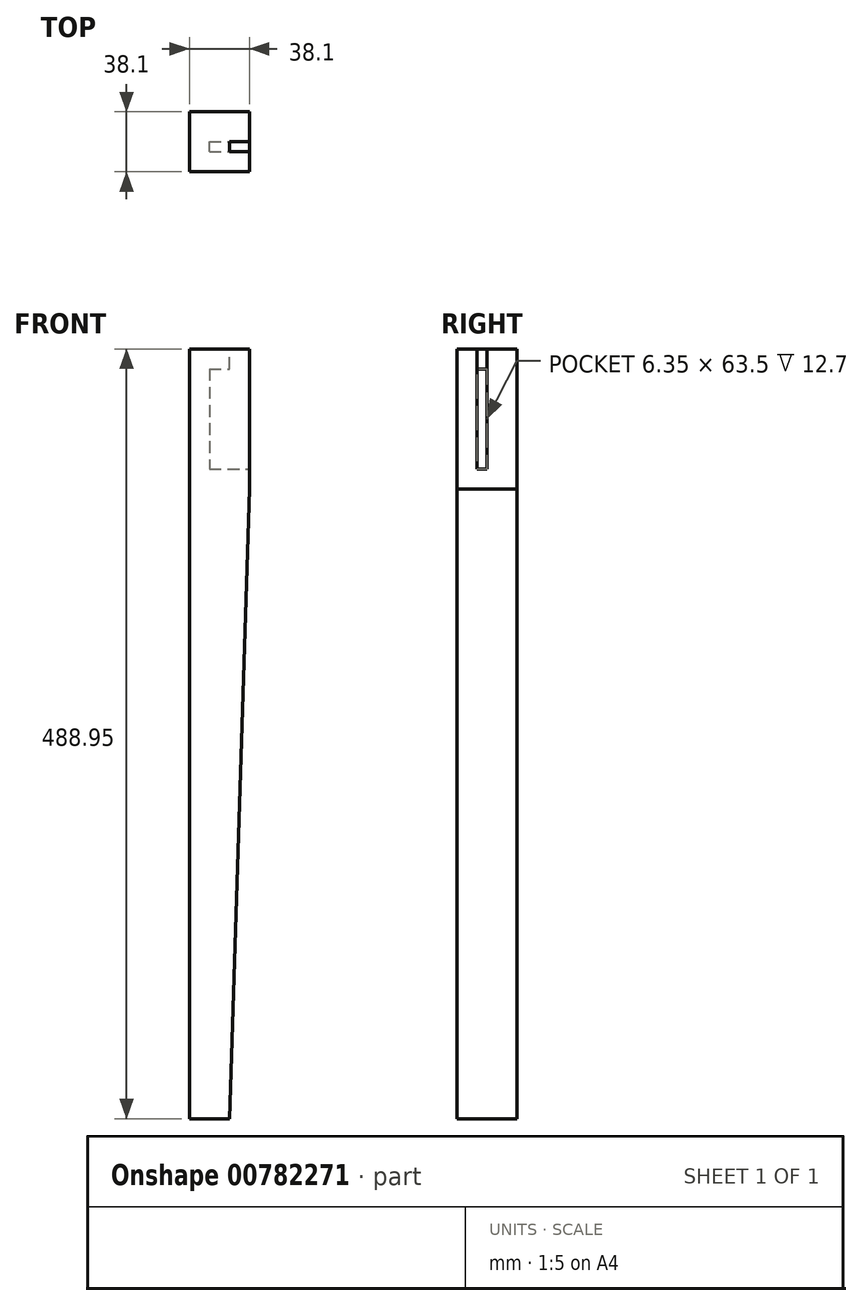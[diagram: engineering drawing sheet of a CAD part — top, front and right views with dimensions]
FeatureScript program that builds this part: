
annotation { "Feature Type Name" : "Feature", "Feature Type Description" : "" }
export const myFeature = defineFeature(function(context is Context, id is Id, definition is map)
    precondition{}
    {
        {
            var Q0;
            Q0=qCreatedBy(makeId("Top.planeOp"),FACE);
            var sketch = newSketch(context, id + "F0", { "sketchPlane" : qUnion([Q0])});
            skLineSegment(sketch, "E0.bottom", {"start": v(-19.05, 19.05) * mm, "end": v(19.05, 19.05) * mm});
            skLineSegment(sketch, "E0.top", {"start": v(-19.05, -19.05) * mm, "end": v(19.05, -19.05) * mm});
            skLineSegment(sketch, "E0.left", {"start": v(-19.05, 19.05) * mm, "end": v(-19.05, -19.05) * mm});
            skLineSegment(sketch, "E0.right", {"start": v(19.05, 19.05) * mm, "end": v(19.05, -19.05) * mm});
            skLineSegment(sketch, "E1", {"start": v(-19.05, 19.05) * mm, "end": v(19.05, -19.05) * mm, "construction": true});
            skSolve(sketch);
        }
        {
            var Q0;
            Q0 = qSketchRegion(id + "F0", true);
            extrude(context, id + "F1", {"entities" : qUnion([Q0]), "oppositeDirection" : true, "depth" : 488.95 * mm, "offsetDistance" : 25.4 * mm});
        }
        {
            var Q0;
            Q0=makeQuery(id+"F1.opExtrude","SWEPT_FACE",FACE,{"disambiguationData":[OSD([sQuery(id+"F0.wireOp",EDGE,"E0.top")])]});
            var sketch = newSketch(context, id + "F2", { "sketchPlane" : qUnion([Q0])});
            skLineSegment(sketch, "E2", {"start": v(19.05, -88.9) * mm, "end": v(6.35, -488.95) * mm});
            skLineSegment(sketch, "E3", {"start": v(6.35, -488.95) * mm, "end": v(19.05, -488.95) * mm});
            skLineSegment(sketch, "E4", {"start": v(19.05, -488.95) * mm, "end": v(19.05, -88.9) * mm});
            skSolve(sketch);
        }
        {
            var Q0;
            Q0 = qSketchRegion(id + "F2", true);
            extrude(context, id + "F3", {"entities" : qUnion([Q0]), "operationType" : NewBodyOperationType.REMOVE, "endBound" : BoundingType.THROUGH_ALL, "oppositeDirection" : true, "depth" : 25.4 * mm, "offsetDistance" : 25.4 * mm});
        }
        {
            var Q0;
            Q0=makeQuery(id+"F1.opExtrude","SWEPT_FACE",FACE,{"disambiguationData":[OSD([sQuery(id+"F0.wireOp",EDGE,"E0.right")])]});
            var sketch = newSketch(context, id + "F4", { "sketchPlane" : qUnion([Q0])});
            skLineSegment(sketch, "E5.top", {"start": v(-6.35, -76.2) * mm, "end": v(0, -76.2) * mm});
            skLineSegment(sketch, "E5.left", {"start": v(-6.35, -12.7) * mm, "end": v(-6.35, -76.2) * mm});
            skLineSegment(sketch, "E5.right", {"start": v(0, -12.7) * mm, "end": v(0, -76.2) * mm});
            skLineSegment(sketch, "E6", {"start": v(-6.35, -12.7) * mm, "end": v(0, -12.7) * mm});
            skLineSegment(sketch, "E7.0", {"start": v(19.05, 0) * mm, "end": v(-19.05, 0) * mm, "construction": true});
            skSolve(sketch);
        }
        {
            var Q0;
            Q0 = qSketchRegion(id + "F4", true);
            var Q1;
            Q1=makeQuery(id+"F1.opExtrude","SWEPT_FACE",FACE,{"disambiguationData":[OSD([sQuery(id+"F0.wireOp",EDGE,"E0.left")])]});
            extrude(context, id + "F5", {"entities" : qUnion([Q0]), "operationType" : NewBodyOperationType.REMOVE, "oppositeDirection" : true, "depth" : 25.4 * mm, "endBoundEntityFace" : qUnion([Q1]), "hasOffset" : true, "offsetDistance" : 12.7 * mm});
        }
        {
            var Q0;
            Q0=makeQuery(id+"F1.opExtrude","SWEPT_FACE",FACE,{"disambiguationData":[OSD([sQuery(id+"F0.wireOp",EDGE,"E0.right")])]});
            var sketch = newSketch(context, id + "F6", { "sketchPlane" : qUnion([Q0])});
            skLineSegment(sketch, "E8.bottom", {"start": v(-6.35, -12.7) * mm, "end": v(0, -12.7) * mm});
            skLineSegment(sketch, "E8.top", {"start": v(-6.35, 0) * mm, "end": v(0, 0) * mm});
            skLineSegment(sketch, "E8.left", {"start": v(-6.35, -12.7) * mm, "end": v(-6.35, 0) * mm});
            skLineSegment(sketch, "E8.right", {"start": v(0, -12.7) * mm, "end": v(0, 0) * mm});
            skSolve(sketch);
        }
        {
            var Q0;
            Q0 = qSketchRegion(id + "F6", true);
            extrude(context, id + "F7", {"entities" : qUnion([Q0]), "operationType" : NewBodyOperationType.REMOVE, "oppositeDirection" : true, "depth" : 12.7 * mm, "offsetDistance" : 25.4 * mm});
        }
        {
            var Q0;
            Q0=qCreatedBy(makeId("Right.planeOp"),FACE);
            var sketch = newSketch(context, id + "F8", { "sketchPlane" : qUnion([Q0])});
            skLineSegment(sketch, "E9", {"start": v(0, 0) * mm, "end": v(0, 68.16) * mm, "construction": true});
            skSolve(sketch);
        }
        {
            var Q0;
            Q0=makeQuery(id+"F1.opExtrude","CAP_VERTEX",VERTEX,{"disambiguationData":[OSD([sQuery(id+"F0.wireOp",EDGE,"E0.top"),sQuery(id+"F0.wireOp",EDGE,"E0.left")])],"isStart":true});
            var Q1;
            Q1=makeQuery(id+"F1.opExtrude","CAP_VERTEX",VERTEX,{"disambiguationData":[OSD([sQuery(id+"F0.wireOp",EDGE,"E0.bottom"),sQuery(id+"F0.wireOp",EDGE,"E0.right")])],"isStart":true});
            var Q2;
            Q2=sQuery(id+"F8.wireOp",VERTEX,"E9.end");
            cPlane(context, id + "F9", {"entities" : qUnion([Q0, Q1, Q2]), "cplaneType" : CPlaneType.THREE_POINT, "offset" : 25.4 * mm, "width" : 152.4 * mm, "height" : 152.4 * mm});
        }
    });
